# Revit family: Loading-Equipment_Dock-levellers_Wayne-Dalton_Edge-dock-leveler
name_source: partatom
category: Specialty Equipment
units: mm (PartAtom-declared; Revit-internal decimal feet)

## family parameters
Cut with Voids When Loaded = No
Host = Face
OmniClass Number = 23.50.70.14.14
Part Type = Normal
Room Calculation Point = No
Round Connector Dimension = Use Diameter
Shared = No

## types (3) — shared parameters
Default Elevation = 4' - 0"
Description = Wayne Dalton DaltonDock™ Edge of Dock Leveler provides smooth, safe path for loading docks and trailers.
Main Material = Metal - Wayne Dalton - Steel
Manufacturer = Wayne Dalton
Product Page URL = https://www.wayne-dalton.com
Product data url = https://www.bimobject.com
Top Plate Material = Metal - Wayne Dalton - Steel Checker Plate
URL = https://www.wayne-dalton.com

## per-type parameters (varying)
| type | Model | Width |
| 66in Wide – Extension Spring – Retractable Pole | Edge Dock E66WD | 5' - 6" |
| 72in Wide – Extension Spring – Retractable Pole | Edge Dock E72WD | 6' - 0" |
| 78in Wide – Extension Spring – Retractable Pole | Edge Dock E78WD | 6' - 6" |

## geometry (parser evidence)
native form markers: Sweep x9
no freeform markers — native parametric forms only
